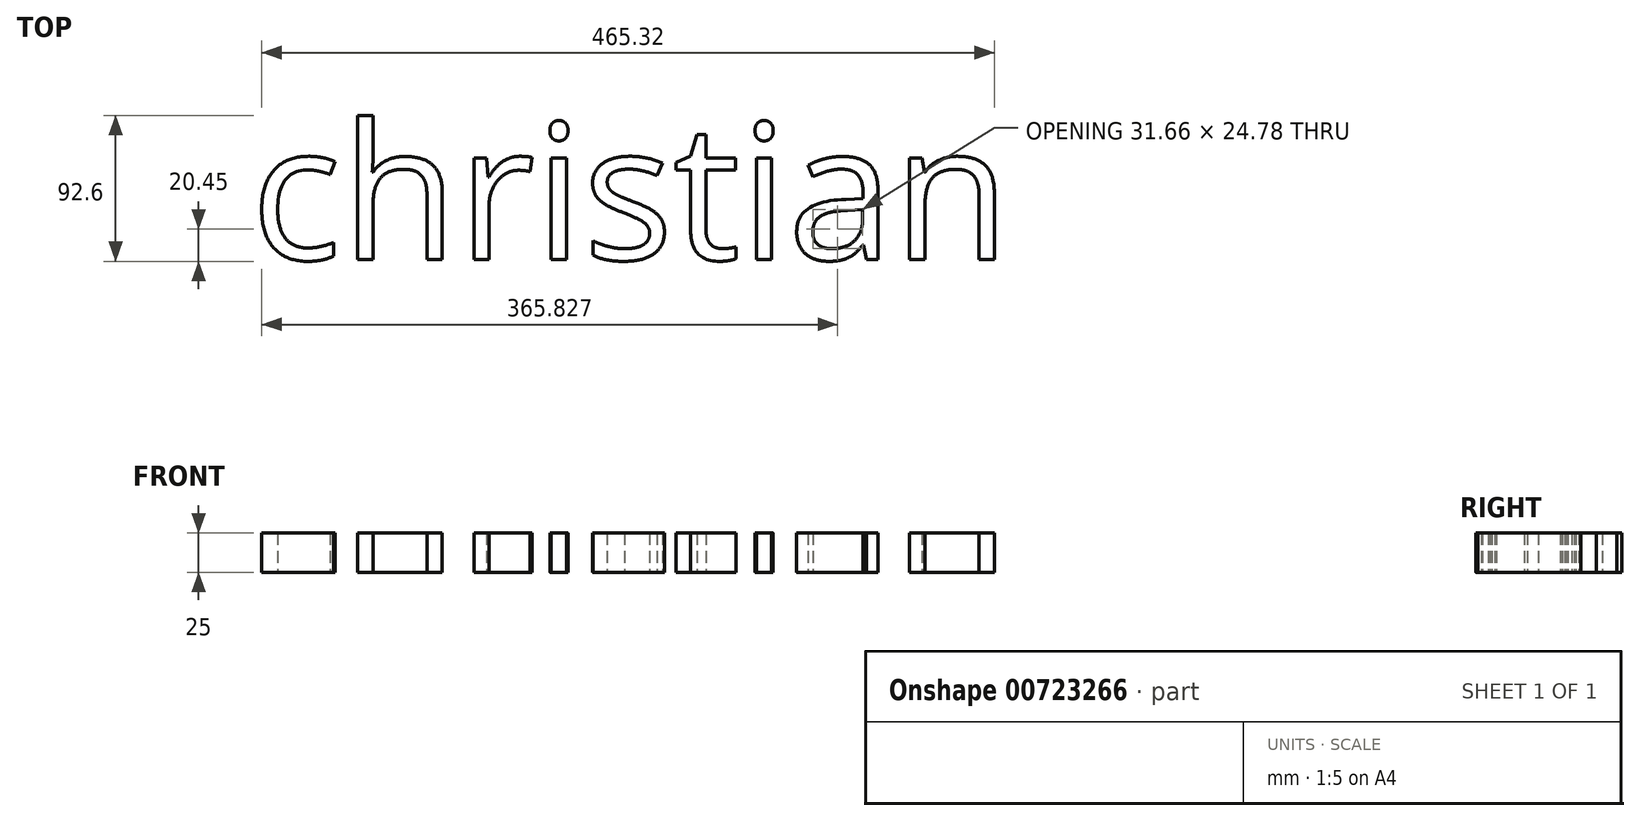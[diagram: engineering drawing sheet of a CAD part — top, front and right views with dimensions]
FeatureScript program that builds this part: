
annotation { "Feature Type Name" : "Feature", "Feature Type Description" : "" }
export const myFeature = defineFeature(function(context is Context, id is Id, definition is map)
    precondition{}
    {
        {
            var Q0;
            Q0=qCreatedBy(makeId("Top.planeOp"),FACE);
            var sketch = newSketch(context, id + "F0", { "sketchPlane" : qUnion([Q0])});
            skText(sketch, "E0", { "text": "christian\n", "fontName": "OpenSans-Regular.ttf"});
            const initialGuessF0  = {"E0": [-0.12908, -0.07128, 1, 0, 0.08663]};
            skSetInitialGuess(sketch, initialGuessF0);
            skSolve(sketch);
        }
        {
            var Q0;
            Q0 = qSketchRegion(id + "F0", true);
            extrude(context, id + "F1", {"entities" : qUnion([Q0]), "depth" : 25 * mm, "offsetDistance" : 25 * mm});
        }
    });
